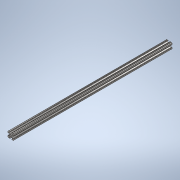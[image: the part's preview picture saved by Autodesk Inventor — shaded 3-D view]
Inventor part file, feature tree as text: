
AUTODESK INVENTOR PART (.ipt)
format: ipt  version: 2020 (Build 240168000, 168)  size: 242,688 bytes
history: native  units: in
note: dims shown in document units (in); Inventor stores cm internally (conversion verified against a paired STEP export)
features: extrude x1, sketch x1
ambient origin geometry x8: Origin, YZ Plane, XZ Plane, XY Plane, X Axis, Y Axis, Z Axis, Center Point
bodies: Solid1 (feature_tree)
feature tree (2):
  extrude  "Extrusion1"  [1 undecoded]
  sketch  "Sketch1"  dims[d0=27.0in d1=0.0in]
note: 1 required parameter value undecoded (feature->parameter linkage not recoverable at this tier; creation-order binding heuristic only, values carry confidence <= 0.55)
